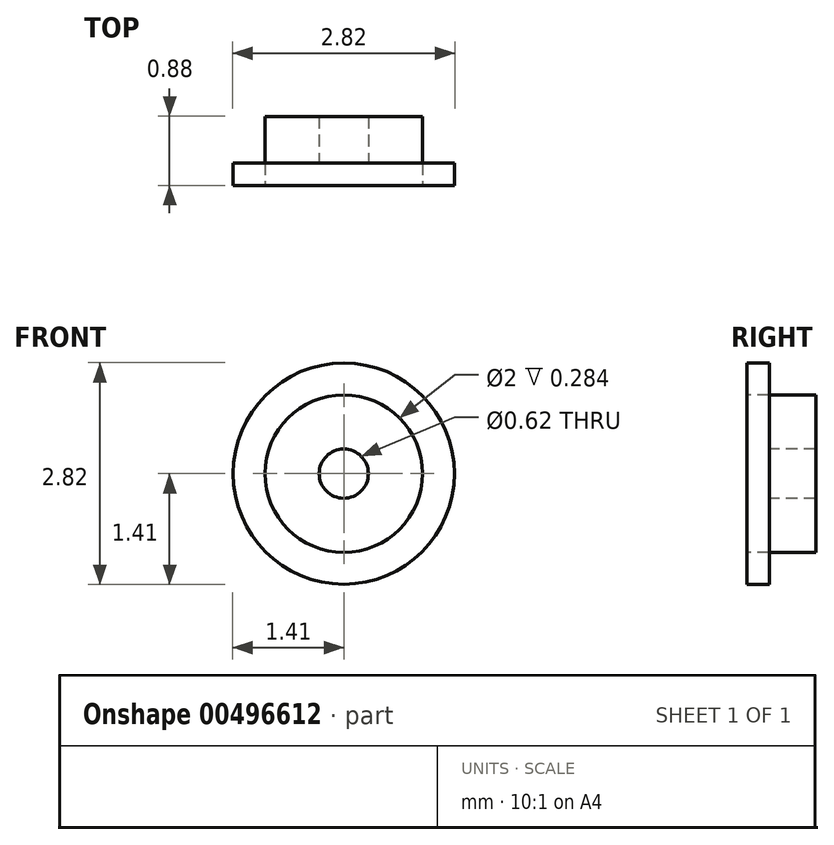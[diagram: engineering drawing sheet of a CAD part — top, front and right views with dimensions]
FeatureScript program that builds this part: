
annotation { "Feature Type Name" : "Feature", "Feature Type Description" : "" }
export const myFeature = defineFeature(function(context is Context, id is Id, definition is map)
    precondition{}
    {
        {
            var Q0;
            Q0=qCreatedBy(makeId("Right.planeOp"),FACE);
            var sketch = newSketch(context, id + "F0", { "sketchPlane" : qUnion([Q0])});
            skLineSegment(sketch, "E0", {"start": v(0, 0) * mm, "end": v(0.87, 0) * mm});
            skLineSegment(sketch, "E1.bottom", {"start": v(0, 0.31) * mm, "end": v(0.28, 0.31) * mm});
            skLineSegment(sketch, "E1.top", {"start": v(0, 1.4) * mm, "end": v(0.28, 1.4) * mm});
            skLineSegment(sketch, "E1.left", {"start": v(0, 0.31) * mm, "end": v(0, 1.4) * mm});
            skLineSegment(sketch, "E1.right", {"start": v(0.28, 0.31) * mm, "end": v(0.28, 1.4) * mm});
            skLineSegment(sketch, "E2.bottom", {"start": v(0, 0.31) * mm, "end": v(0.88, 0.31) * mm});
            skLineSegment(sketch, "E2.top", {"start": v(0, 1) * mm, "end": v(0.88, 1) * mm});
            skLineSegment(sketch, "E2.left", {"start": v(0, 0.31) * mm, "end": v(0, 1) * mm});
            skLineSegment(sketch, "E2.right", {"start": v(0.88, 0.31) * mm, "end": v(0.87, 1) * mm});
            skLineSegment(sketch, "E3.MirrorCS", {"start": v(0, -0.31) * mm, "end": v(0.28, -0.31) * mm});
            skLineSegment(sketch, "E4.MirrorCS", {"start": v(0, -1.4) * mm, "end": v(0.28, -1.4) * mm});
            skLineSegment(sketch, "E5.MirrorCS", {"start": v(0, -0.31) * mm, "end": v(0, -1.4) * mm});
            skLineSegment(sketch, "E6.MirrorCS", {"start": v(0.28, -0.31) * mm, "end": v(0.28, -1.4) * mm});
            skLineSegment(sketch, "E7.MirrorCS", {"start": v(0.88, -0.31) * mm, "end": v(0.88, -1) * mm});
            skLineSegment(sketch, "E8.MirrorCS", {"start": v(0, -1) * mm, "end": v(0.88, -1) * mm});
            skLineSegment(sketch, "E9.MirrorCS", {"start": v(0, -0.31) * mm, "end": v(0.88, -0.31) * mm});
            skLineSegment(sketch, "E10.MirrorCS", {"start": v(0, -0.31) * mm, "end": v(0, -1) * mm});
            skSolve(sketch);
        }
        {
            var Q0;
            {var subQ0=sQuery(id+"F0.wireOp",EDGE,"E1.top");Q0=makeQuery(id+"F0.imprint","IMPRINT",FACE,{"disambiguationData":[TD([[makeQuery(id+"F0.imprint","IMPRINT",EDGE,{"derivedFrom":subQ0}),-1.0]])]});}
            var Q1;
            {var subQ5=sQuery(id+"F0.wireOp",EDGE,"E2.left");Q1=makeQuery(id+"F0.imprint","IMPRINT",FACE,{"disambiguationData":[TD([[makeQuery(id+"F0.imprint","IMPRINT",EDGE,{"derivedFrom":subQ5}),-1.0]])]});}
            var Q2;
            {var subQ5=sQuery(id+"F0.wireOp",EDGE,"E2.right");Q2=makeQuery(id+"F0.imprint","IMPRINT",FACE,{"disambiguationData":[TD([[makeQuery(id+"F0.imprint","IMPRINT",EDGE,{"derivedFrom":subQ5}),1.0]])]});}
            var Q3;
            Q3=sQuery(id+"F0.wireOp",EDGE,"E0");
            revolve(context, id + "F1", {"entities" : qUnion([Q0, Q1, Q2]), "axis" : qUnion([Q3]), "revolveType" : RevolveType.FULL});
        }
    });
